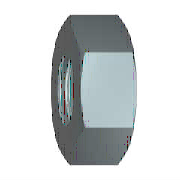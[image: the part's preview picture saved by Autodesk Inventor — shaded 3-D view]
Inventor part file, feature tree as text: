
AUTODESK INVENTOR PART (.ipt)
format: ipt  version: 2013 (Build 170138000, 138)  size: 171,520 bytes
history: native  units: mm (DEFAULTED — no unit token found)
features: sketch x3, chamfer x1, hole x1, other x1, plane x1
ambient origin geometry x7: Origin, YZ Plane, XZ Plane, X Axis, Y Axis, Z Axis, Center Point
bodies: Solid1 (feature_tree), Body (feature_tree)
feature tree (7):
  chamfer  "Chamfer1"  Distance=4.363323mm
  hole  "Thread"  [1 undecoded]
  other  "Work Axis1"
  plane  "Work Plane1"
  sketch  "Sketch1"  dims[d0=9.237604mm]
  sketch  "Sketch2"  dims[d1=4.7mm]
  sketch  "Sketch3"  dims[d2=0.0mm d3=4.363323mm d4=4.363323mm d5=8.0mm d6=8.0mm d7=90.0deg d25=4.134mm d26=6.0mm d27=4.0mm d28=2.0mm d29=14.3117mm d30=8.0mm d31=20.594885mm d8=0.433013mm d9=30.0deg d10=0.433013mm d11=30.0deg d13=0.0mm d14=0.0mm d39=0.0mm d40=0.433013mm d41=0.433013mm d42=0.0mm]
note: 1 required parameter value undecoded (feature->parameter linkage not recoverable at this tier; creation-order binding heuristic only, values carry confidence <= 0.55)
